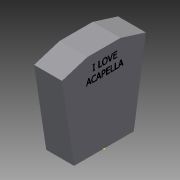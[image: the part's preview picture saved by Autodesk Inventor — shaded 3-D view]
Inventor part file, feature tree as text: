
AUTODESK INVENTOR PART (.ipt)
format: ipt  version: 2015 SP1 (Build 190203100, 203)  size: 80,384 bytes
history: native  units: in
note: dims shown in document units (in); Inventor stores cm internally (conversion verified against a paired STEP export)
features: sketch x3, extrude x1
ambient origin geometry x8: Origin, YZ Plane, XZ Plane, XY Plane, X Axis, Y Axis, Z Axis, Center Point
bodies: Solid1 (feature_tree)
feature tree (4):
  extrude  "Extrusion1"  Depth=6.7in
  sketch  "Sketch2"  dims[d6=15.0in]
  sketch  "Sketch3"  dims[d7=22.0in d8=20.0in d9=21.1in d10=7.0in d11=0.0in]
  sketch  "Sketch1"  dims[d4=6.7in d5=6.7in]
